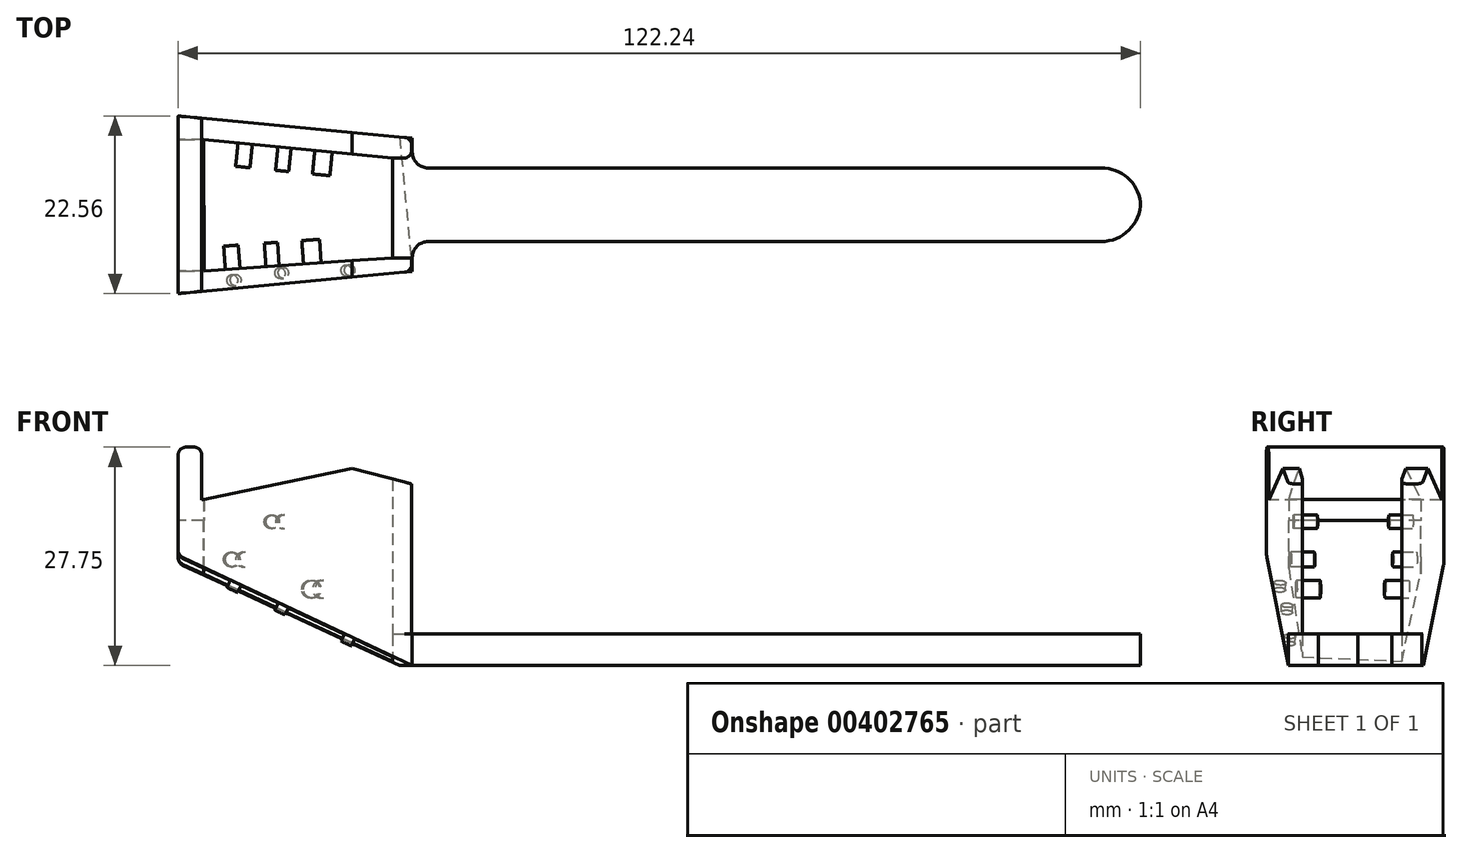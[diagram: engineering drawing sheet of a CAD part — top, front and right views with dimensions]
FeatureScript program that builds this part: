
annotation { "Feature Type Name" : "Feature", "Feature Type Description" : "" }
export const myFeature = defineFeature(function(context is Context, id is Id, definition is map)
    precondition{}
    {
        {
            var Q0;
            Q0=qCreatedBy(makeId("Top.planeOp"),FACE);
            var sketch = newSketch(context, id + "F0", { "sketchPlane" : qUnion([Q0])});
            skLineSegment(sketch, "E0.top", {"start": v(46.25, 4.67) * mm, "end": v(-46.25, 4.68) * mm});
            skPoint(sketch, "E0.middle", {"position": v(0, 0) * mm});
            skLineSegment(sketch, "E1", {"start": v(-46.25, 4.67) * mm, "end": v(-46.25, 8.48) * mm});
            skLineSegment(sketch, "E2", {"start": v(-46.25, 8.48) * mm, "end": v(-76, 11.27) * mm});
            skLineSegment(sketch, "E3", {"start": v(-76, 11.27) * mm, "end": v(-76, 0) * mm});
            skPoint(sketch, "E0.bottom.end.orphan", {"position": v(-46.25, -4.68) * mm});
            skPoint(sketch, "E0.left.start.orphan", {"position": v(46.25, -4.67) * mm});
            skLineSegment(sketch, "E4", {"start": v(46.25, 0) * mm, "end": v(46.25, 4.68) * mm});
            skPoint(sketch, "E5.orphan", {"position": v(-46.25, 0) * mm});
            skLineSegment(sketch, "E6", {"start": v(-76, 0) * mm, "end": v(46.25, 0) * mm});
            skLineSegment(sketch, "E7.MirrorCS", {"start": v(-76, -11.27) * mm, "end": v(-76, 0) * mm});
            skLineSegment(sketch, "E8.MirrorCS", {"start": v(-46.25, -8.48) * mm, "end": v(-76, -11.27) * mm});
            skLineSegment(sketch, "E9.MirrorCS", {"start": v(-46.25, -4.67) * mm, "end": v(-46.25, -8.48) * mm});
            skLineSegment(sketch, "E10.MirrorCS", {"start": v(46.25, -4.68) * mm, "end": v(-46.25, -4.67) * mm});
            skLineSegment(sketch, "E11.MirrorCS", {"start": v(46.25, 0) * mm, "end": v(46.25, -4.68) * mm});
            skSolve(sketch);
        }
        {
            var Q0;
            Q0=makeQuery(id+"F0.imprint","IMPRINT",FACE,{"disambiguationData":[TD([[makeQuery(id+"F0.imprint","IMPRINT",EDGE,{"derivedFrom":sQuery(id+"F0.wireOp",EDGE,"E0.top")}),1.0]])]});
            var Q1;
            Q1=makeQuery(id+"F0.imprint","IMPRINT",FACE,{"disambiguationData":[TD([[makeQuery(id+"F0.imprint","IMPRINT",EDGE,{"derivedFrom":sQuery(id+"F0.wireOp",EDGE,"E6")}),-1.0]])]});
            extrude(context, id + "F1", {"entities" : qUnion([Q0, Q1]), "depth" : 27.75 * mm});
        }
        {
            var Q0;
            Q0=qCreatedBy(makeId("Front.planeOp"),FACE);
            var sketch = newSketch(context, id + "F2", { "sketchPlane" : qUnion([Q0])});
            skLineSegment(sketch, "E12.bottom", {"start": v(46.25, 4) * mm, "end": v(-46.34, 4) * mm});
            skLineSegment(sketch, "E12.top", {"start": v(46.25, 28.3) * mm, "end": v(-46.34, 28.3) * mm});
            skLineSegment(sketch, "E12.left", {"start": v(46.25, 4) * mm, "end": v(46.25, 28.3) * mm});
            skLineSegment(sketch, "E12.right", {"start": v(-46.34, 4) * mm, "end": v(-46.34, 28.3) * mm});
            skSolve(sketch);
        }
        {
            var Q0;
            Q0 = qSketchRegion(id + "F2", true);
            extrude(context, id + "F3", {"entities" : qUnion([Q0]), "operationType" : NewBodyOperationType.REMOVE, "endBound" : BoundingType.SYMMETRIC, "oppositeDirection" : true, "depth" : 25 * mm});
        }
        {
            var Q0;
            Q0=makeQuery(id+"F1.opExtrude","SWEPT_FACE",FACE,{"disambiguationData":[OSD([sQuery(id+"F0.wireOp",EDGE,"E8.MirrorCS")])]});
            var sketch = newSketch(context, id + "F4", { "sketchPlane" : qUnion([Q0])});
            skLineSegment(sketch, "E13", {"start": v(-76.71, 0) * mm, "end": v(-76.71, 14) * mm});
            skLineSegment(sketch, "E14", {"start": v(-76.71, 14) * mm, "end": v(-46.84, 0) * mm});
            skLineSegment(sketch, "E15", {"start": v(-46.84, 0) * mm, "end": v(-76.71, 0) * mm});
            skSolve(sketch);
        }
        {
            var Q0;
            Q0 = qSketchRegion(id + "F4", true);
            var Q1;
            Q1=makeQuery(id+"F1.opExtrude","SWEPT_FACE",FACE,{"disambiguationData":[OSD([sQuery(id+"F0.wireOp",EDGE,"E2")])]});
            extrude(context, id + "F5", {"entities" : qUnion([Q0]), "operationType" : NewBodyOperationType.REMOVE, "endBound" : BoundingType.UP_TO_SURFACE, "oppositeDirection" : true, "endBoundEntityFace" : qUnion([Q1]), "depth" : 25 * mm});
        }
        {
            var Q0;
            Q0=qCreatedBy(makeId("Front.planeOp"),FACE);
            var sketch = newSketch(context, id + "F6", { "sketchPlane" : qUnion([Q0])});
            skLineSegment(sketch, "E16", {"start": v(-73, 26.1) * mm, "end": v(-73, 21.05) * mm});
            skLineSegment(sketch, "E17", {"start": v(-73, 21.05) * mm, "end": v(-53.88, 25.05) * mm});
            skLineSegment(sketch, "E18", {"start": v(-53.88, 25.05) * mm, "end": v(-41.55, 21.8) * mm});
            skLineSegment(sketch, "E19", {"start": v(-41.55, 21.8) * mm, "end": v(-41.55, 28.4) * mm});
            skLineSegment(sketch, "E20", {"start": v(-41.55, 28.4) * mm, "end": v(-73, 28.05) * mm});
            skLineSegment(sketch, "E21", {"start": v(-73, 28.05) * mm, "end": v(-73, 26.1) * mm});
            skSolve(sketch);
        }
        {
            var Q0;
            Q0 = qSketchRegion(id + "F6", true);
            extrude(context, id + "F7", {"entities" : qUnion([Q0]), "operationType" : NewBodyOperationType.REMOVE, "endBound" : BoundingType.SYMMETRIC, "oppositeDirection" : true, "depth" : 25 * mm});
        }
        {
            var Q0;
            Q0=qCreatedBy(makeId("Top.planeOp"),FACE);
            var sketch = newSketch(context, id + "F8", { "sketchPlane" : qUnion([Q0])});
            skLineSegment(sketch, "E22", {"start": v(-72.7, -8.44) * mm, "end": v(-48.76, -6.74) * mm});
            skLineSegment(sketch, "E23", {"start": v(-48.76, -6.74) * mm, "end": v(-48.76, 5.91) * mm});
            skLineSegment(sketch, "E24", {"start": v(-48.76, 5.91) * mm, "end": v(-72.78, 8.31) * mm});
            skLineSegment(sketch, "E25", {"start": v(-72.78, 8.31) * mm, "end": v(-72.7, -8.44) * mm});
            skSolve(sketch);
        }
        {
            var Q0;
            Q0 = qSketchRegion(id + "F8", true);
            extrude(context, id + "F9", {"entities" : qUnion([Q0]), "operationType" : NewBodyOperationType.REMOVE, "endBound" : BoundingType.THROUGH_ALL, "depth" : 25 * mm});
        }
        {
            var Q0;
            Q0=makeQuery(id+"F3.boolean.opBoolean","COPY",FACE,{"derivedFrom":makeQuery(id+"F3.opExtrude","SWEPT_FACE",FACE,{"disambiguationData":[OSD([sQuery(id+"F2.wireOp",EDGE,"E12.right")])]})});
            var sketch = newSketch(context, id + "F10", { "sketchPlane" : qUnion([Q0])});
            skPoint(sketch, "E26.0", {"position": v(-6.74, 23.7) * mm});
            skPoint(sketch, "E27.0", {"position": v(5.91, 23.7) * mm});
            skLineSegment(sketch, "E28", {"start": v(-6.74, 23.7) * mm, "end": v(-6.74, 4) * mm});
            skLineSegment(sketch, "E29", {"start": v(-6.74, 23.7) * mm, "end": v(5.91, 23.7) * mm});
            skLineSegment(sketch, "E30", {"start": v(5.91, 23.7) * mm, "end": v(5.91, 4) * mm});
            skLineSegment(sketch, "E31", {"start": v(5.91, 4) * mm, "end": v(-6.74, 4) * mm});
            skSolve(sketch);
        }
        {
            var Q0;
            Q0 = qSketchRegion(id + "F10", true);
            extrude(context, id + "F11", {"entities" : qUnion([Q0]), "operationType" : NewBodyOperationType.REMOVE, "oppositeDirection" : true, "depth" : 25 * mm});
        }
        {
            var Q0;
            Q0=makeQuery(id+"F1.opExtrude","SWEPT_FACE",FACE,{"disambiguationData":[OSD([sQuery(id+"F0.wireOp",EDGE,"E3"),sQuery(id+"F0.wireOp",EDGE,"E7.MirrorCS")])]});
            var sketch = newSketch(context, id + "F12", { "sketchPlane" : qUnion([Q0])});
            skPoint(sketch, "E32.0", {"position": v(-8.31, 11.64) * mm});
            skPoint(sketch, "E33.0", {"position": v(8.44, 12.34) * mm});
            skLineSegment(sketch, "E34.bottom", {"start": v(-8.31, 11.64) * mm, "end": v(8.44, 11.64) * mm});
            skLineSegment(sketch, "E34.top", {"start": v(-8.31, 18.43) * mm, "end": v(8.44, 18.43) * mm});
            skLineSegment(sketch, "E34.left", {"start": v(-8.31, 11.64) * mm, "end": v(-8.31, 18.43) * mm});
            skLineSegment(sketch, "E34.right", {"start": v(8.44, 11.64) * mm, "end": v(8.44, 18.43) * mm});
            skSolve(sketch);
        }
        {
            var Q0;
            Q0 = qSketchRegion(id + "F12", true);
            extrude(context, id + "F13", {"entities" : qUnion([Q0]), "operationType" : NewBodyOperationType.REMOVE, "endBound" : BoundingType.UP_TO_NEXT, "oppositeDirection" : true, "depth" : 25 * mm});
        }
        {
            var Q0;
            Q0=makeQuery(id+"F1.opExtrude","SWEPT_EDGE",EDGE,{"disambiguationData":[OSD([sQuery(id+"F0.wireOp",EDGE,"E10.MirrorCS"),sQuery(id+"F0.wireOp",EDGE,"E11.MirrorCS")])]});
            fillet(context, id + "F14", {"entities" : qUnion([Q0]), "radius" : 5 * mm, "tangentPropagation" : true, "allowEdgeOverflow" : false});
        }
        {
            var Q0;
            Q0=makeQuery(id+"F1.opExtrude","SWEPT_EDGE",EDGE,{"disambiguationData":[OSD([sQuery(id+"F0.wireOp",EDGE,"E0.top"),sQuery(id+"F0.wireOp",EDGE,"E4")])]});
            fillet(context, id + "F15", {"entities" : qUnion([Q0]), "radius" : 5 * mm, "tangentPropagation" : true, "allowEdgeOverflow" : false});
        }
        {
            var Q0;
            Q0=makeQuery(id+"F1.opExtrude","SWEPT_EDGE",EDGE,{"disambiguationData":[OSD([sQuery(id+"F0.wireOp",EDGE,"E9.MirrorCS"),sQuery(id+"F0.wireOp",EDGE,"E10.MirrorCS")])]});
            fillet(context, id + "F16", {"entities" : qUnion([Q0]), "radius" : 2 * mm, "tangentPropagation" : true, "allowEdgeOverflow" : false});
        }
        {
            var Q0;
            Q0=makeQuery(id+"F1.opExtrude","SWEPT_EDGE",EDGE,{"disambiguationData":[OSD([sQuery(id+"F0.wireOp",EDGE,"E0.top"),sQuery(id+"F0.wireOp",EDGE,"E1")])]});
            fillet(context, id + "F17", {"entities" : qUnion([Q0]), "radius" : 2 * mm, "tangentPropagation" : true, "allowEdgeOverflow" : false});
        }
        {
            var Q0;
            Q0=makeQuery(id+"F1.opExtrude","CAP_EDGE",EDGE,{"disambiguationData":[OSD([sQuery(id+"F0.wireOp",EDGE,"E3"),sQuery(id+"F0.wireOp",EDGE,"E7.MirrorCS")])],"isStart":false});
            fillet(context, id + "F18", {"entities" : qUnion([Q0]), "radius" : 1 * mm, "tangentPropagation" : true, "allowEdgeOverflow" : false});
        }
        {
            var Q0;
            Q0=makeQuery(id+"F7.boolean.opBoolean","INTERSECT",EDGE,{"derivedFrom":[makeQuery(id+"F1.opExtrude","CAP_FACE",FACE,{"disambiguationData":[OSD([sQuery(id+"F0.wireOp",EDGE,"E0.top"),sQuery(id+"F0.wireOp",EDGE,"E1"),sQuery(id+"F0.wireOp",EDGE,"E2"),sQuery(id+"F0.wireOp",EDGE,"E3"),sQuery(id+"F0.wireOp",EDGE,"E4"),sQuery(id+"F0.wireOp",EDGE,"E7.MirrorCS"),sQuery(id+"F0.wireOp",EDGE,"E8.MirrorCS"),sQuery(id+"F0.wireOp",EDGE,"E9.MirrorCS"),sQuery(id+"F0.wireOp",EDGE,"E10.MirrorCS"),sQuery(id+"F0.wireOp",EDGE,"E11.MirrorCS")])],"isStart":false}),makeQuery(id+"F7.opExtrude","SWEPT_FACE",FACE,{"disambiguationData":[OSD([sQuery(id+"F6.wireOp",EDGE,"E16"),sQuery(id+"F6.wireOp",EDGE,"E21")])]})]});
            fillet(context, id + "F19", {"entities" : qUnion([Q0]), "radius" : 1 * mm, "tangentPropagation" : true, "allowEdgeOverflow" : false});
        }
        {
            var Q0;
            {var subQ0=makeQuery(id+"F1.opExtrude","SWEPT_FACE",FACE,{"disambiguationData":[OSD([sQuery(id+"F0.wireOp",EDGE,"E3"),sQuery(id+"F0.wireOp",EDGE,"E7.MirrorCS")])]});var subQ1=makeQuery(id+"F5.opExtrude","SWEPT_FACE",FACE,{"disambiguationData":[OSD([sQuery(id+"F4.wireOp",EDGE,"E14")])]});Q0=makeQuery(id+"F13.boolean.opBoolean","SPLIT",EDGE,{"disambiguationData":[TD([makeQuery(id+"F1.opExtrude","SWEPT_FACE",FACE,{"disambiguationData":[OSD([sQuery(id+"F0.wireOp",EDGE,"E8.MirrorCS")])]})])],"derivedFrom":makeQuery(id+"F5.boolean.opBoolean","INTERSECT",EDGE,{"derivedFrom":[subQ0,subQ1]})});}
            fillet(context, id + "F20", {"entities" : qUnion([Q0]), "radius" : 1 * mm, "tangentPropagation" : true, "allowEdgeOverflow" : false});
        }
        {
            var Q0;
            {var subQ0=makeQuery(id+"F1.opExtrude","SWEPT_FACE",FACE,{"disambiguationData":[OSD([sQuery(id+"F0.wireOp",EDGE,"E3"),sQuery(id+"F0.wireOp",EDGE,"E7.MirrorCS")])]});var subQ1=makeQuery(id+"F5.opExtrude","SWEPT_FACE",FACE,{"disambiguationData":[OSD([sQuery(id+"F4.wireOp",EDGE,"E14")])]});Q0=makeQuery(id+"F13.boolean.opBoolean","SPLIT",EDGE,{"disambiguationData":[TD([makeQuery(id+"F1.opExtrude","SWEPT_FACE",FACE,{"disambiguationData":[OSD([sQuery(id+"F0.wireOp",EDGE,"E2")])]})])],"derivedFrom":makeQuery(id+"F5.boolean.opBoolean","INTERSECT",EDGE,{"derivedFrom":[subQ0,subQ1]})});}
            fillet(context, id + "F21", {"entities" : qUnion([Q0]), "radius" : 1 * mm, "tangentPropagation" : true, "allowEdgeOverflow" : false});
        }
        {
            var Q0;
            Q0=makeQuery(id+"F3.boolean.opBoolean","INTERSECT",EDGE,{"derivedFrom":[makeQuery(id+"F1.opExtrude","SWEPT_FACE",FACE,{"disambiguationData":[OSD([sQuery(id+"F0.wireOp",EDGE,"E8.MirrorCS")])]}),makeQuery(id+"F3.opExtrude","SWEPT_FACE",FACE,{"disambiguationData":[OSD([sQuery(id+"F2.wireOp",EDGE,"E12.right")])]})]});
            fillet(context, id + "F22", {"entities" : qUnion([Q0]), "radius" : 1 * mm, "tangentPropagation" : true, "allowEdgeOverflow" : false});
        }
        {
            var Q0;
            Q0=makeQuery(id+"F3.boolean.opBoolean","INTERSECT",EDGE,{"derivedFrom":[makeQuery(id+"F1.opExtrude","SWEPT_FACE",FACE,{"disambiguationData":[OSD([sQuery(id+"F0.wireOp",EDGE,"E2")])]}),makeQuery(id+"F3.opExtrude","SWEPT_FACE",FACE,{"disambiguationData":[OSD([sQuery(id+"F2.wireOp",EDGE,"E12.right")])]})]});
            fillet(context, id + "F23", {"entities" : qUnion([Q0]), "radius" : 1 * mm, "tangentPropagation" : true, "allowEdgeOverflow" : false});
        }
        {
            var Q0;
            Q0=makeQuery(id+"F11.boolean.opBoolean","COPY",EDGE,{"derivedFrom":makeQuery(id+"F11.opExtrude","CAP_EDGE",EDGE,{"disambiguationData":[OSD([sQuery(id+"F10.wireOp",EDGE,"E30")])],"isStart":true})});
            var Q1;
            Q1=makeQuery(id+"F11.boolean.opBoolean","COPY",EDGE,{"derivedFrom":makeQuery(id+"F11.opExtrude","CAP_EDGE",EDGE,{"disambiguationData":[OSD([sQuery(id+"F10.wireOp",EDGE,"E28")])],"isStart":true})});
            fillet(context, id + "F24", {"entities" : qUnion([Q0, Q1]), "radius" : 1 * mm, "tangentPropagation" : true, "allowEdgeOverflow" : false});
        }
        {
            var Q0;
            Q0=makeQuery(id+"F9.boolean.opBoolean","COPY",FACE,{"derivedFrom":makeQuery(id+"F9.opExtrude","SWEPT_FACE",FACE,{"disambiguationData":[OSD([sQuery(id+"F8.wireOp",EDGE,"E22")])]})});
            var sketch = newSketch(context, id + "F25", { "sketchPlane" : qUnion([Q0])});
            skCircle(sketch, "E35", {"center": v(64.38, 18.26) * mm, "radius": 0.85 * mm});
            skCircle(sketch, "E36", {"center": v(69.48, 13.47) * mm, "radius": 0.93 * mm});
            skCircle(sketch, "E37", {"center": v(59.33, 9.7) * mm, "radius": 1.13 * mm});
            skSolve(sketch);
        }
        {
            var Q0;
            Q0 = qSketchRegion(id + "F25", true);
            extrude(context, id + "F26", {"entities" : qUnion([Q0]), "operationType" : NewBodyOperationType.ADD, "depth" : 3 * mm});
        }
        {
            var Q0;
            Q0=makeQuery(id+"F9.boolean.opBoolean","COPY",FACE,{"derivedFrom":makeQuery(id+"F9.opExtrude","SWEPT_FACE",FACE,{"disambiguationData":[OSD([sQuery(id+"F8.wireOp",EDGE,"E24")])]})});
            var sketch = newSketch(context, id + "F27", { "sketchPlane" : qUnion([Q0])});
            skEllipse(sketch, "E38.0", {"center": v(-62.9, 18.26) * mm, "majorRadius": 0.85 * mm, "minorRadius": 0.84 * mm, "majorAxis": v(0, 1)});
            skEllipse(sketch, "E38.1", {"center": v(-67.92, 13.47) * mm, "majorRadius": 0.93 * mm, "minorRadius": 0.92 * mm, "majorAxis": v(0, 1)});
            skEllipse(sketch, "E38.2", {"center": v(-57.91, 9.7) * mm, "majorRadius": 1.13 * mm, "minorRadius": 1.1 * mm, "majorAxis": v(0, 1)});
            skEllipse(sketch, "E38.3", {"center": v(-62.9, 18.26) * mm, "majorRadius": 0.85 * mm, "minorRadius": 0.84 * mm, "majorAxis": v(0, 1)});
            skSolve(sketch);
        }
        {
            var Q0;
            Q0 = qSketchRegion(id + "F27", true);
            extrude(context, id + "F28", {"entities" : qUnion([Q0]), "operationType" : NewBodyOperationType.ADD, "depth" : 3 * mm});
        }
        {
            var Q0;
            Q0=makeQuery(id+"F5.boolean.opBoolean","COPY",FACE,{"derivedFrom":makeQuery(id+"F5.opExtrude","SWEPT_FACE",FACE,{"disambiguationData":[OSD([sQuery(id+"F4.wireOp",EDGE,"E14")])]})});
            var sketch = newSketch(context, id + "F29", { "sketchPlane" : qUnion([Q0])});
            skCircle(sketch, "E39", {"center": v(-66.52, 10.02) * mm, "radius": 0.74 * mm});
            skCircle(sketch, "E40", {"center": v(-59.84, 8.97) * mm, "radius": 0.71 * mm});
            skCircle(sketch, "E41", {"center": v(-50.55, 8.47) * mm, "radius": 0.72 * mm});
            skSolve(sketch);
        }
        {
            var Q0;
            Q0 = qSketchRegion(id + "F29", true);
            extrude(context, id + "F30", {"entities" : qUnion([Q0]), "operationType" : NewBodyOperationType.ADD, "depth" : 1 * mm});
        }
    });
